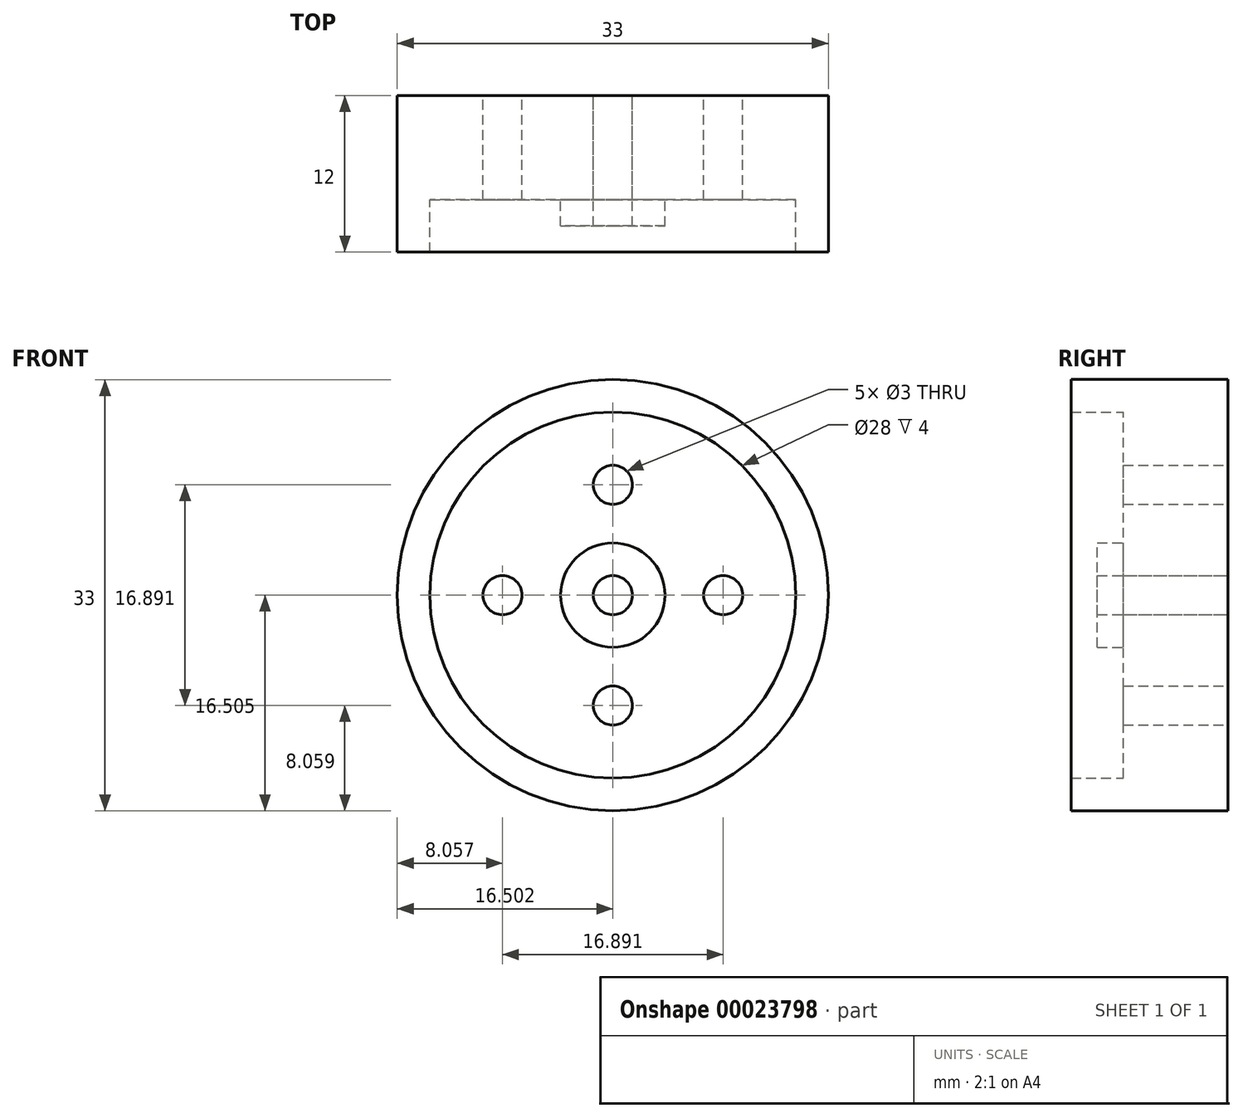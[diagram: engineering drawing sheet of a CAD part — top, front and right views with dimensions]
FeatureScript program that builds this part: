
annotation { "Feature Type Name" : "Feature", "Feature Type Description" : "" }
export const myFeature = defineFeature(function(context is Context, id is Id, definition is map)
    precondition{}
    {
        {
            var Q0;
            Q0=qCreatedBy(makeId("Front.planeOp"),FACE);
            var sketch = newSketch(context, id + "F0", { "sketchPlane" : qUnion([Q0])});
            skCircle(sketch, "E0", {"center": v(-19.6, 6.02) * mm, "radius": 4 * mm});
            skCircle(sketch, "E1", {"center": v(-19.6, 6.02) * mm, "radius": 14 * mm});
            skCircle(sketch, "E2", {"center": v(-19.6, 6.02) * mm, "radius": 16.5 * mm});
            skLineSegment(sketch, "E3", {"start": v(-19.6, 6.02) * mm, "end": v(-19.6, -52.63) * mm});
            skPoint(sketch, "E4.orphan", {"position": v(-13.9, 18.81) * mm});
            skCircle(sketch, "E5.2.0", {"center": v(-19.6, 14.47) * mm, "radius": 1.5 * mm});
            skCircle(sketch, "E6", {"center": v(-19.6, -2.42) * mm, "radius": 1.5 * mm});
            skCircle(sketch, "E5.3.0", {"center": v(-28.05, 6.02) * mm, "radius": 1.5 * mm});
            skCircle(sketch, "E5.1.0", {"center": v(-11.16, 6.02) * mm, "radius": 1.5 * mm});
            skCircle(sketch, "E7", {"center": v(-19.6, 6.02) * mm, "radius": 1.5 * mm});
            skSolve(sketch);
        }
        {
            var Q0;
            Q0=makeQuery(id+"F0.imprint","IMPRINT",FACE,{"disambiguationData":[TD([[makeQuery(id+"F0.imprint","IMPRINT",EDGE,{"derivedFrom":sQuery(id+"F0.wireOp",EDGE,"E1")}),-1.0]])]});
            extrude(context, id + "F1", {"entities" : qUnion([Q0]), "depth" : 12 * mm});
        }
        {
            var Q0;
            Q0=makeQuery(id+"F0.imprint","IMPRINT",FACE,{"disambiguationData":[TD([[makeQuery(id+"F0.imprint","IMPRINT",EDGE,{"derivedFrom":sQuery(id+"F0.wireOp",EDGE,"E0")}),-1.0]])]});
            extrude(context, id + "F2", {"entities" : qUnion([Q0]), "operationType" : NewBodyOperationType.ADD, "depth" : 8 * mm});
        }
        {
            var Q0;
            Q0=makeQuery(id+"F0.imprint","IMPRINT",FACE,{"disambiguationData":[TD([[makeQuery(id+"F0.imprint","IMPRINT",EDGE,{"derivedFrom":sQuery(id+"F0.wireOp",EDGE,"E0")}),1.0]])]});
            extrude(context, id + "F3", {"entities" : qUnion([Q0]), "operationType" : NewBodyOperationType.ADD, "depth" : 10 * mm});
        }
    });
